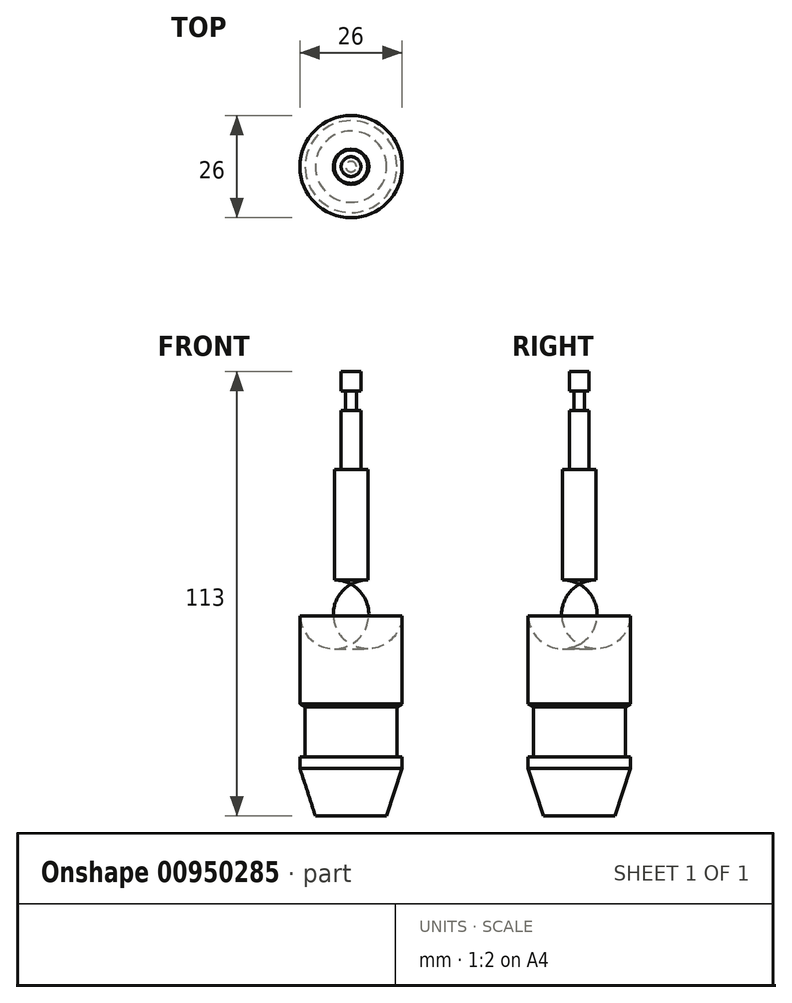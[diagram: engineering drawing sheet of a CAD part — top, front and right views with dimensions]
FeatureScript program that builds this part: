
annotation { "Feature Type Name" : "Feature", "Feature Type Description" : "" }
export const myFeature = defineFeature(function(context is Context, id is Id, definition is map)
    precondition{}
    {
        {
            var Q0;
            Q0=qCreatedBy(makeId("Front.planeOp"),FACE);
            var sketch = newSketch(context, id + "F0", { "sketchPlane" : qUnion([Q0])});
            skLineSegment(sketch, "E0", {"start": v(0, 56.18) * mm, "end": v(0, -48.13) * mm, "construction": true});
            skLineSegment(sketch, "E1", {"start": v(0, 45.94) * mm, "end": v(-2.5, 45.94) * mm});
            skLineSegment(sketch, "E2", {"start": v(-2.5, 45.94) * mm, "end": v(-2.5, 40.94) * mm});
            skLineSegment(sketch, "E3", {"start": v(-2.5, 40.94) * mm, "end": v(-1.34, 40.94) * mm});
            skLineSegment(sketch, "E4", {"start": v(-1.34, 40.94) * mm, "end": v(-1.34, 35.94) * mm});
            skLineSegment(sketch, "E5", {"start": v(-1.34, 35.94) * mm, "end": v(-2.5, 35.94) * mm});
            skLineSegment(sketch, "E6", {"start": v(-2.5, 35.94) * mm, "end": v(-2.5, 20.94) * mm});
            skLineSegment(sketch, "E7", {"start": v(-2.5, 20.94) * mm, "end": v(-4.25, 20.94) * mm});
            skLineSegment(sketch, "E8", {"start": v(-4.25, 20.94) * mm, "end": v(-4.25, -7.06) * mm});
            skArc(sketch, "E9", {"start": v(-4.25, -7.06) * mm, "mid": v(-10.6, -9.77) * mm, "end": v(-13, -16.24) * mm});
            skLineSegment(sketch, "E10", {"start": v(-13, -16.24) * mm, "end": v(-13, -38.54) * mm});
            skLineSegment(sketch, "E11", {"start": v(-13, -38.54) * mm, "end": v(-11.67, -39.38) * mm});
            skLineSegment(sketch, "E12", {"start": v(-11.67, -39.38) * mm, "end": v(-11.67, -52.06) * mm});
            skLineSegment(sketch, "E13", {"start": v(-11.67, -52.06) * mm, "end": v(-13, -52.06) * mm});
            skLineSegment(sketch, "E14", {"start": v(-13, -52.06) * mm, "end": v(-13, -54.9) * mm});
            skLineSegment(sketch, "E15", {"start": v(-13, -54.9) * mm, "end": v(-9.05, -67.06) * mm});
            skLineSegment(sketch, "E16", {"start": v(-9.05, -67.06) * mm, "end": v(0, -67.06) * mm});
            skLineSegment(sketch, "E17", {"start": v(0, -67.06) * mm, "end": v(0, 45.94) * mm});
            skSolve(sketch);
        }
        {
            var Q0;
            Q0 = qSketchRegion(id + "F0", true);
            var Q1;
            Q1=sQuery(id+"F0.wireOp",EDGE,"E17");
            revolve(context, id + "F1", {"surfaceOperationType" : NewSurfaceOperationType.NEW, "entities" : qUnion([Q0]), "axis" : qUnion([Q1]), "revolveType" : RevolveType.FULL});
        }
    });
